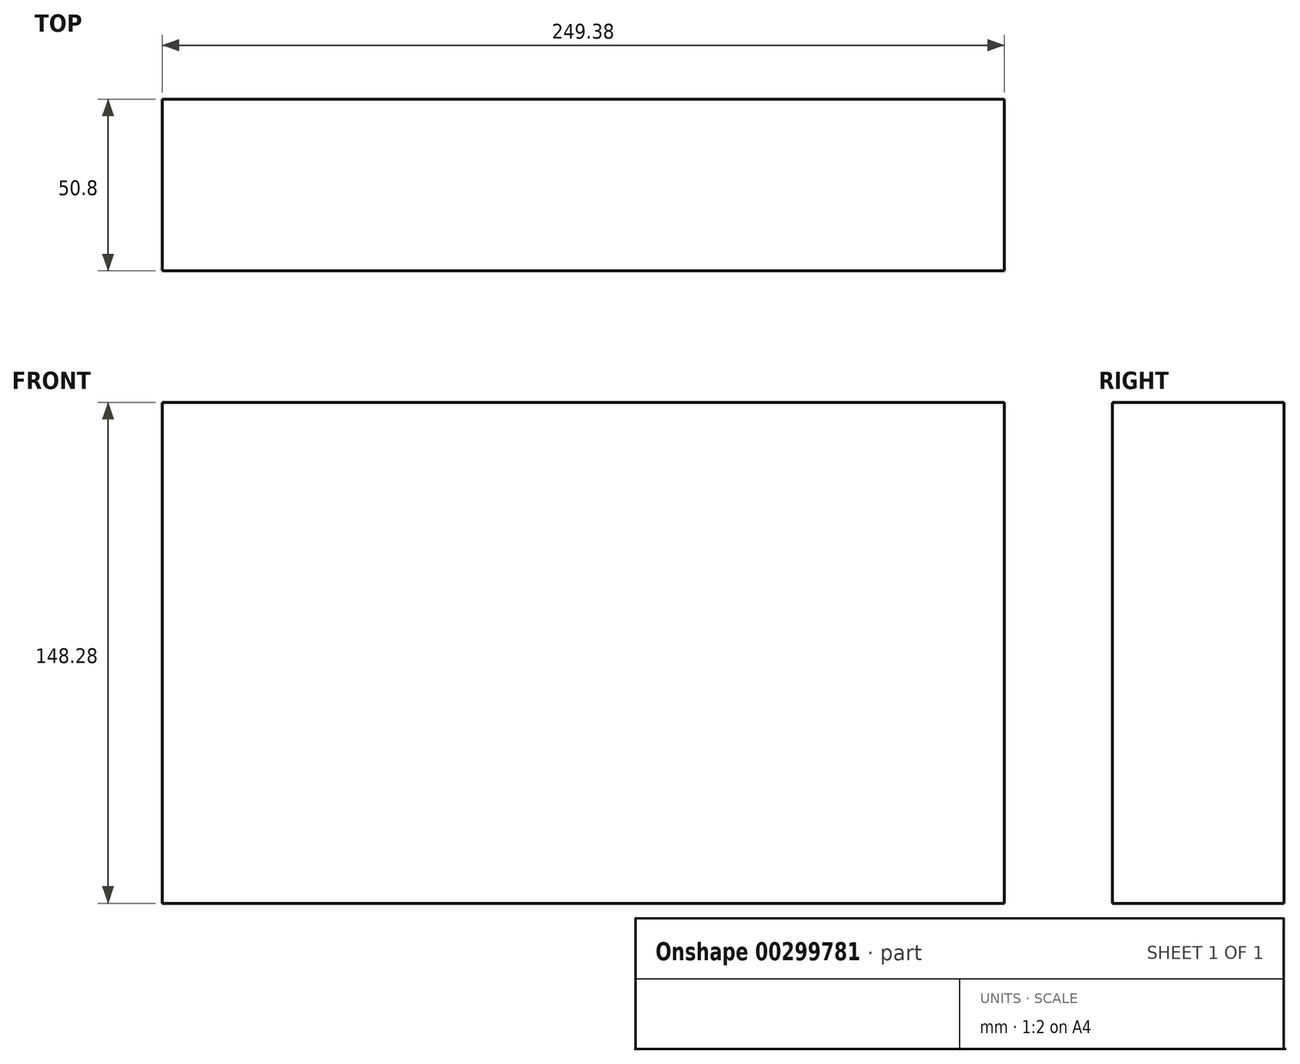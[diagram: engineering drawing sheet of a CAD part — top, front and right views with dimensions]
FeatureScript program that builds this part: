
annotation { "Feature Type Name" : "Feature", "Feature Type Description" : "" }
export const myFeature = defineFeature(function(context is Context, id is Id, definition is map)
    precondition{}
    {
        {
            var Q0;
            Q0=qCreatedBy(makeId("Front.planeOp"),FACE);
            var sketch = newSketch(context, id + "F0", { "sketchPlane" : qUnion([Q0])});
            skLineSegment(sketch, "E0.bottom", {"start": v(-124.69, 74.14) * mm, "end": v(124.69, 74.14) * mm});
            skLineSegment(sketch, "E0.top", {"start": v(-124.69, -74.14) * mm, "end": v(124.69, -74.14) * mm});
            skLineSegment(sketch, "E0.left", {"start": v(-124.69, 74.14) * mm, "end": v(-124.69, -74.14) * mm});
            skLineSegment(sketch, "E0.right", {"start": v(124.69, 74.14) * mm, "end": v(124.69, -74.14) * mm});
            skPoint(sketch, "E0.middle", {"position": v(0, 0) * mm});
            skSolve(sketch);
        }
        {
            var Q0;
            Q0 = qSketchRegion(id + "F0", true);
            extrude(context, id + "F1", {"entities" : qUnion([Q0]), "depth" : 50.8 * mm});
        }
    });
